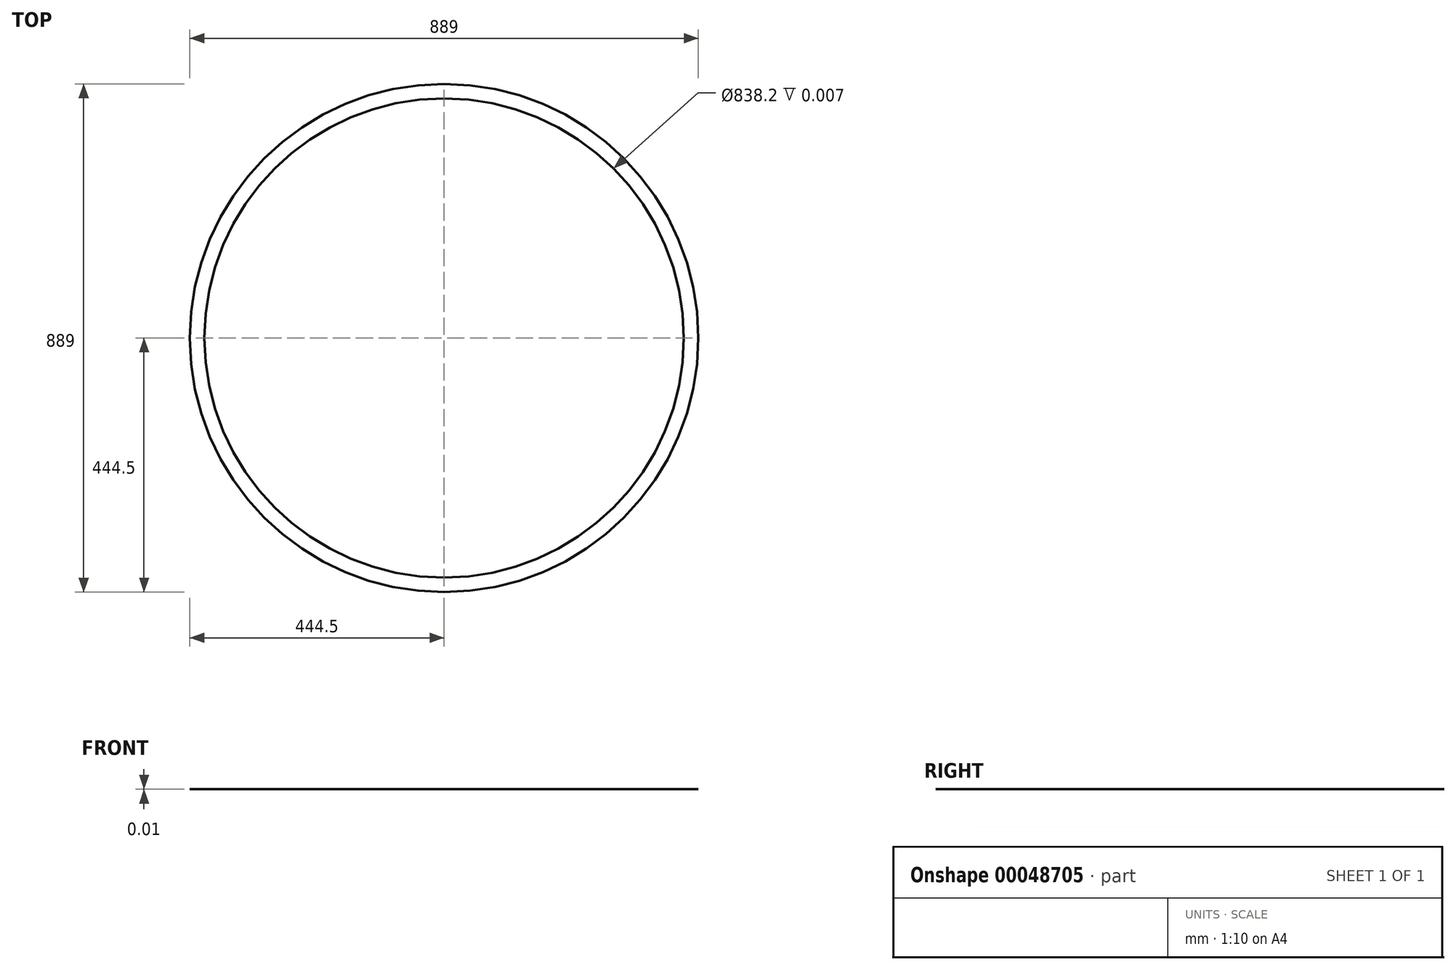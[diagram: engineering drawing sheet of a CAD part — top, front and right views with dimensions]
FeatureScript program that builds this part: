
annotation { "Feature Type Name" : "Feature", "Feature Type Description" : "" }
export const myFeature = defineFeature(function(context is Context, id is Id, definition is map)
    precondition{}
    {
        {
            var Q0;
            Q0=qCreatedBy(makeId("Top.planeOp"),FACE);
            var sketch = newSketch(context, id + "F0", { "sketchPlane" : qUnion([Q0])});
            skCircle(sketch, "E0", {"center": v(0, 0) * mm, "radius": 444.5 * mm});
            skCircle(sketch, "E1", {"center": v(0, 0) * mm, "radius": 419.1 * mm});
            skSolve(sketch);
        }
        {
            var Q0;
            Q0 = qSketchRegion(id + "F0", true);
            extrude(context, id + "F1", {"entities" : qUnion([Q0]), "depth" : 3 / 457.2 * mm});
        }
    });
